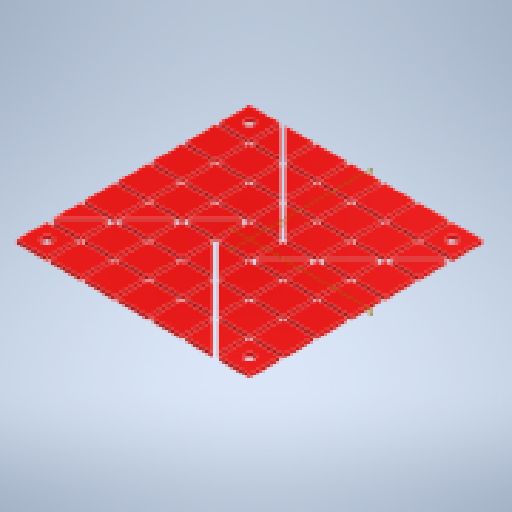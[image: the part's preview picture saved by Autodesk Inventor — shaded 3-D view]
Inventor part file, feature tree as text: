
AUTODESK INVENTOR PART (.ipt)
format: ipt  version: 2024 (Build 280153000, 153)  size: 388,608 bytes
history: native  units: in
note: dims shown in document units (in); Inventor stores cm internally (conversion verified against a paired STEP export)
features: extrude x2, plane x2, sketch x1, other x1, pattern_circular x1
ambient origin geometry x8: Origin, YZ Plane, XZ Plane, XY Plane, X Axis, Y Axis, Z Axis, Center Point
bodies: Solid1 (feature_tree)
feature tree (7):
  sketch  "Sketch1"  dims[d0=3.75in d1=3.75in d2=3.1496in d4=0.5357in d5=3.1496in d7=0.5357in d10=0.0312in d11=0.0312in d12=0.0312in d13=0.0312in d14=0.0312in d15=0.0312in d16=0.0312in d17=0.0312in d18=0.0312in d19=0.0312in d20=0.0312in d21=0.0312in d22=0.0312in d23=0.0312in d24=0.0312in d25=0.0312in d26=0.0312in d27=0.0312in d28=0.0312in d29=0.0625in d30=0.0in d31=0.0625in d32=0.0in d33=1.5748in d34=360.0deg d36=0.17in d37=0.2679in d38=0.2679in]
  extrude  "Extrusion1"  Depth=0.0625in
  extrude  "Extrusion2"  Depth=0.5357in
  other  "Work Axis1"
  pattern_circular  "Circular Pattern1"  [2 undecoded]
  plane  "Work Plane1"
  plane  "Work Plane2"
note: 2 required parameter values undecoded (feature->parameter linkage not recoverable at this tier; creation-order binding heuristic only, values carry confidence <= 0.55)
